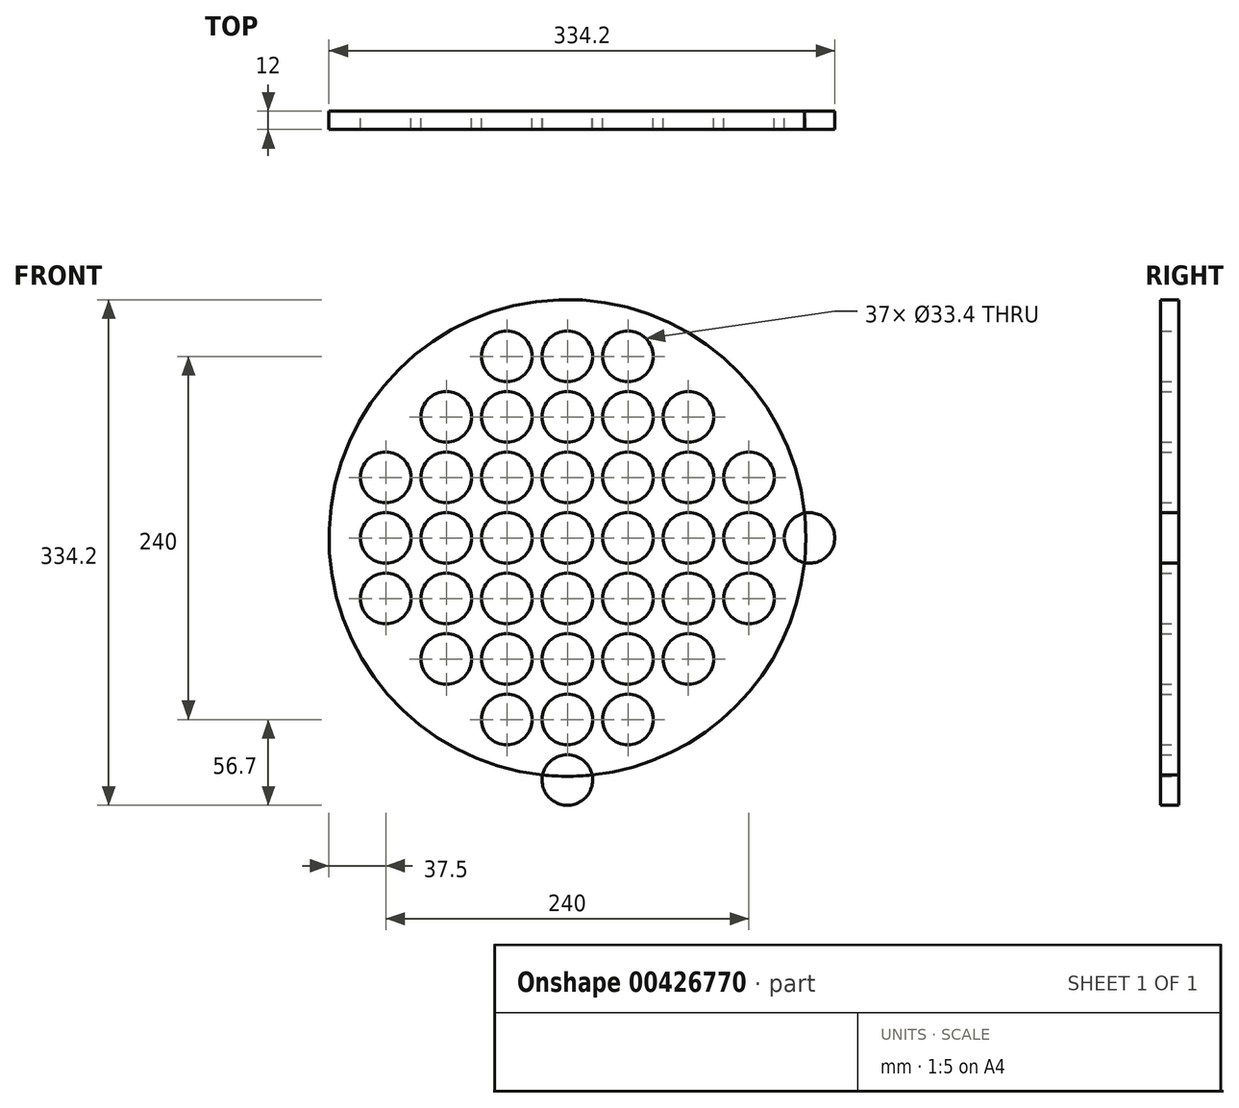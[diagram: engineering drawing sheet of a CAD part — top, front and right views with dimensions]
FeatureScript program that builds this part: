
annotation { "Feature Type Name" : "Feature", "Feature Type Description" : "" }
export const myFeature = defineFeature(function(context is Context, id is Id, definition is map)
    precondition{}
    {
        {
            var Q0;
            Q0=qCreatedBy(makeId("Front.planeOp"),FACE);
            var sketch = newSketch(context, id + "F0", { "sketchPlane" : qUnion([Q0])});
            skCircle(sketch, "E0", {"center": v(-240, -240) * mm, "radius": 16.7 * mm});
            skCircle(sketch, "E1.0.1.0", {"center": v(-240, -200) * mm, "radius": 16.7 * mm});
            skCircle(sketch, "E1.0.2.0", {"center": v(-240, -160) * mm, "radius": 16.7 * mm});
            skCircle(sketch, "E1.0.3.0", {"center": v(-240, -120) * mm, "radius": 16.7 * mm});
            skCircle(sketch, "E1.0.4.0", {"center": v(-240, -80) * mm, "radius": 16.7 * mm});
            skCircle(sketch, "E1.0.5.0", {"center": v(-240, -40) * mm, "radius": 16.7 * mm});
            skCircle(sketch, "E1.0.6.0", {"center": v(-240, 0) * mm, "radius": 16.7 * mm});
            skCircle(sketch, "E1.0.7.0", {"center": v(-240, 40) * mm, "radius": 16.7 * mm});
            skCircle(sketch, "E1.0.8.0", {"center": v(-240, 80) * mm, "radius": 16.7 * mm});
            skCircle(sketch, "E1.0.9.0", {"center": v(-240, 120) * mm, "radius": 16.7 * mm});
            skCircle(sketch, "E1.1.0.0", {"center": v(-200, -240) * mm, "radius": 16.7 * mm});
            skCircle(sketch, "E1.1.1.0", {"center": v(-200, -200) * mm, "radius": 16.7 * mm});
            skCircle(sketch, "E1.1.2.0", {"center": v(-200, -160) * mm, "radius": 16.7 * mm});
            skCircle(sketch, "E1.1.3.0", {"center": v(-200, -120) * mm, "radius": 16.7 * mm});
            skCircle(sketch, "E1.1.4.0", {"center": v(-200, -80) * mm, "radius": 16.7 * mm});
            skCircle(sketch, "E1.1.5.0", {"center": v(-200, -40) * mm, "radius": 16.7 * mm});
            skCircle(sketch, "E1.1.6.0", {"center": v(-200, 0) * mm, "radius": 16.7 * mm});
            skCircle(sketch, "E1.1.7.0", {"center": v(-200, 40) * mm, "radius": 16.7 * mm});
            skCircle(sketch, "E1.1.8.0", {"center": v(-200, 80) * mm, "radius": 16.7 * mm});
            skCircle(sketch, "E1.1.9.0", {"center": v(-200, 120) * mm, "radius": 16.7 * mm});
            skCircle(sketch, "E1.2.0.0", {"center": v(-160, -240) * mm, "radius": 16.7 * mm});
            skCircle(sketch, "E1.2.1.0", {"center": v(-160, -200) * mm, "radius": 16.7 * mm});
            skCircle(sketch, "E1.2.2.0", {"center": v(-160, -160) * mm, "radius": 16.7 * mm});
            skCircle(sketch, "E1.2.3.0", {"center": v(-160, -120) * mm, "radius": 16.7 * mm});
            skCircle(sketch, "E1.2.4.0", {"center": v(-160, -80) * mm, "radius": 16.7 * mm});
            skCircle(sketch, "E1.2.5.0", {"center": v(-160, -40) * mm, "radius": 16.7 * mm});
            skCircle(sketch, "E1.2.6.0", {"center": v(-160, 0) * mm, "radius": 16.7 * mm});
            skCircle(sketch, "E1.2.7.0", {"center": v(-160, 40) * mm, "radius": 16.7 * mm});
            skCircle(sketch, "E1.2.8.0", {"center": v(-160, 80) * mm, "radius": 16.7 * mm});
            skCircle(sketch, "E1.2.9.0", {"center": v(-160, 120) * mm, "radius": 16.7 * mm});
            skCircle(sketch, "E1.3.0.0", {"center": v(-120, -240) * mm, "radius": 16.7 * mm});
            skCircle(sketch, "E1.3.1.0", {"center": v(-120, -200) * mm, "radius": 16.7 * mm});
            skCircle(sketch, "E1.3.2.0", {"center": v(-120, -160) * mm, "radius": 16.7 * mm});
            skCircle(sketch, "E1.3.3.0", {"center": v(-120, -120) * mm, "radius": 16.7 * mm});
            skCircle(sketch, "E1.3.4.0", {"center": v(-120, -80) * mm, "radius": 16.7 * mm});
            skCircle(sketch, "E1.3.5.0", {"center": v(-120, -40) * mm, "radius": 16.7 * mm});
            skCircle(sketch, "E1.3.6.0", {"center": v(-120, 0) * mm, "radius": 16.7 * mm});
            skCircle(sketch, "E1.3.7.0", {"center": v(-120, 40) * mm, "radius": 16.7 * mm});
            skCircle(sketch, "E1.3.8.0", {"center": v(-120, 80) * mm, "radius": 16.7 * mm});
            skCircle(sketch, "E1.3.9.0", {"center": v(-120, 120) * mm, "radius": 16.7 * mm});
            skCircle(sketch, "E1.4.0.0", {"center": v(-80, -240) * mm, "radius": 16.7 * mm});
            skCircle(sketch, "E1.4.1.0", {"center": v(-80, -200) * mm, "radius": 16.7 * mm});
            skCircle(sketch, "E1.4.2.0", {"center": v(-80, -160) * mm, "radius": 16.7 * mm});
            skCircle(sketch, "E1.4.3.0", {"center": v(-80, -120) * mm, "radius": 16.7 * mm});
            skCircle(sketch, "E1.4.4.0", {"center": v(-80, -80) * mm, "radius": 16.7 * mm});
            skCircle(sketch, "E1.4.5.0", {"center": v(-80, -40) * mm, "radius": 16.7 * mm});
            skCircle(sketch, "E1.4.6.0", {"center": v(-80, 0) * mm, "radius": 16.7 * mm});
            skCircle(sketch, "E1.4.7.0", {"center": v(-80, 40) * mm, "radius": 16.7 * mm});
            skCircle(sketch, "E1.4.8.0", {"center": v(-80, 80) * mm, "radius": 16.7 * mm});
            skCircle(sketch, "E1.4.9.0", {"center": v(-80, 120) * mm, "radius": 16.7 * mm});
            skCircle(sketch, "E1.5.0.0", {"center": v(-40, -240) * mm, "radius": 16.7 * mm});
            skCircle(sketch, "E1.5.1.0", {"center": v(-40, -200) * mm, "radius": 16.7 * mm});
            skCircle(sketch, "E1.5.2.0", {"center": v(-40, -160) * mm, "radius": 16.7 * mm});
            skCircle(sketch, "E1.5.3.0", {"center": v(-40, -120) * mm, "radius": 16.7 * mm});
            skCircle(sketch, "E1.5.4.0", {"center": v(-40, -80) * mm, "radius": 16.7 * mm});
            skCircle(sketch, "E1.5.5.0", {"center": v(-40, -40) * mm, "radius": 16.7 * mm});
            skCircle(sketch, "E1.5.6.0", {"center": v(-40, 0) * mm, "radius": 16.7 * mm});
            skCircle(sketch, "E1.5.7.0", {"center": v(-40, 40) * mm, "radius": 16.7 * mm});
            skCircle(sketch, "E1.5.8.0", {"center": v(-40, 80) * mm, "radius": 16.7 * mm});
            skCircle(sketch, "E1.5.9.0", {"center": v(-40, 120) * mm, "radius": 16.7 * mm});
            skCircle(sketch, "E1.6.0.0", {"center": v(0, -240) * mm, "radius": 16.7 * mm});
            skCircle(sketch, "E1.6.1.0", {"center": v(0, -200) * mm, "radius": 16.7 * mm});
            skCircle(sketch, "E1.6.2.0", {"center": v(0, -160) * mm, "radius": 16.7 * mm});
            skCircle(sketch, "E1.6.3.0", {"center": v(0, -120) * mm, "radius": 16.7 * mm});
            skCircle(sketch, "E1.6.4.0", {"center": v(0, -80) * mm, "radius": 16.7 * mm});
            skCircle(sketch, "E1.6.5.0", {"center": v(0, -40) * mm, "radius": 16.7 * mm});
            skCircle(sketch, "E1.6.6.0", {"center": v(0, 0) * mm, "radius": 16.7 * mm});
            skCircle(sketch, "E1.6.7.0", {"center": v(0, 40) * mm, "radius": 16.7 * mm});
            skCircle(sketch, "E1.6.8.0", {"center": v(0, 80) * mm, "radius": 16.7 * mm});
            skCircle(sketch, "E1.6.9.0", {"center": v(0, 120) * mm, "radius": 16.7 * mm});
            skCircle(sketch, "E1.7.0.0", {"center": v(40, -240) * mm, "radius": 16.7 * mm});
            skCircle(sketch, "E1.7.1.0", {"center": v(40, -200) * mm, "radius": 16.7 * mm});
            skCircle(sketch, "E1.7.2.0", {"center": v(40, -160) * mm, "radius": 16.7 * mm});
            skCircle(sketch, "E1.7.3.0", {"center": v(40, -120) * mm, "radius": 16.7 * mm});
            skCircle(sketch, "E1.7.4.0", {"center": v(40, -80) * mm, "radius": 16.7 * mm});
            skCircle(sketch, "E1.7.5.0", {"center": v(40, -40) * mm, "radius": 16.7 * mm});
            skCircle(sketch, "E1.7.6.0", {"center": v(40, 0) * mm, "radius": 16.7 * mm});
            skCircle(sketch, "E1.7.7.0", {"center": v(40, 40) * mm, "radius": 16.7 * mm});
            skCircle(sketch, "E1.7.8.0", {"center": v(40, 80) * mm, "radius": 16.7 * mm});
            skCircle(sketch, "E1.7.9.0", {"center": v(40, 120) * mm, "radius": 16.7 * mm});
            skCircle(sketch, "E1.8.0.0", {"center": v(80, -240) * mm, "radius": 16.7 * mm});
            skCircle(sketch, "E1.8.1.0", {"center": v(80, -200) * mm, "radius": 16.7 * mm});
            skCircle(sketch, "E1.8.2.0", {"center": v(80, -160) * mm, "radius": 16.7 * mm});
            skCircle(sketch, "E1.8.3.0", {"center": v(80, -120) * mm, "radius": 16.7 * mm});
            skCircle(sketch, "E1.8.4.0", {"center": v(80, -80) * mm, "radius": 16.7 * mm});
            skCircle(sketch, "E1.8.5.0", {"center": v(80, -40) * mm, "radius": 16.7 * mm});
            skCircle(sketch, "E1.8.6.0", {"center": v(80, 0) * mm, "radius": 16.7 * mm});
            skCircle(sketch, "E1.8.7.0", {"center": v(80, 40) * mm, "radius": 16.7 * mm});
            skCircle(sketch, "E1.8.8.0", {"center": v(80, 80) * mm, "radius": 16.7 * mm});
            skCircle(sketch, "E1.8.9.0", {"center": v(80, 120) * mm, "radius": 16.7 * mm});
            skCircle(sketch, "E1.9.0.0", {"center": v(120, -240) * mm, "radius": 16.7 * mm});
            skCircle(sketch, "E1.9.1.0", {"center": v(120, -200) * mm, "radius": 16.7 * mm});
            skCircle(sketch, "E1.9.2.0", {"center": v(120, -160) * mm, "radius": 16.7 * mm});
            skCircle(sketch, "E1.9.3.0", {"center": v(120, -120) * mm, "radius": 16.7 * mm});
            skCircle(sketch, "E1.9.4.0", {"center": v(120, -80) * mm, "radius": 16.7 * mm});
            skCircle(sketch, "E1.9.5.0", {"center": v(120, -40) * mm, "radius": 16.7 * mm});
            skCircle(sketch, "E1.9.6.0", {"center": v(120, 0) * mm, "radius": 16.7 * mm});
            skCircle(sketch, "E1.9.7.0", {"center": v(120, 40) * mm, "radius": 16.7 * mm});
            skCircle(sketch, "E1.9.8.0", {"center": v(120, 80) * mm, "radius": 16.7 * mm});
            skCircle(sketch, "E1.9.9.0", {"center": v(120, 120) * mm, "radius": 16.7 * mm});
            skLineSegment(sketch, "E1.direction1", {"start": v(-240, -240) * mm, "end": v(-200, -240) * mm, "construction": true});
            skLineSegment(sketch, "E1.direction2", {"start": v(-240, -240) * mm, "end": v(-240, -200) * mm, "construction": true});
            skCircle(sketch, "E2.0.0.10", {"center": v(-240, 160) * mm, "radius": 16.7 * mm});
            skCircle(sketch, "E2.0.0.11", {"center": v(-240, 200) * mm, "radius": 16.7 * mm});
            skCircle(sketch, "E2.0.1.10", {"center": v(-200, 160) * mm, "radius": 16.7 * mm});
            skCircle(sketch, "E2.0.1.11", {"center": v(-200, 200) * mm, "radius": 16.7 * mm});
            skCircle(sketch, "E2.0.2.10", {"center": v(-160, 160) * mm, "radius": 16.7 * mm});
            skCircle(sketch, "E2.0.2.11", {"center": v(-160, 200) * mm, "radius": 16.7 * mm});
            skCircle(sketch, "E2.0.3.10", {"center": v(-120, 160) * mm, "radius": 16.7 * mm});
            skCircle(sketch, "E2.0.3.11", {"center": v(-120, 200) * mm, "radius": 16.7 * mm});
            skCircle(sketch, "E2.0.4.10", {"center": v(-80, 160) * mm, "radius": 16.7 * mm});
            skCircle(sketch, "E2.0.4.11", {"center": v(-80, 200) * mm, "radius": 16.7 * mm});
            skCircle(sketch, "E2.0.5.10", {"center": v(-40, 160) * mm, "radius": 16.7 * mm});
            skCircle(sketch, "E2.0.5.11", {"center": v(-40, 200) * mm, "radius": 16.7 * mm});
            skCircle(sketch, "E2.0.6.10", {"center": v(0, 160) * mm, "radius": 16.7 * mm});
            skCircle(sketch, "E2.0.6.11", {"center": v(0, 200) * mm, "radius": 16.7 * mm});
            skCircle(sketch, "E2.0.7.10", {"center": v(40, 160) * mm, "radius": 16.7 * mm});
            skCircle(sketch, "E2.0.7.11", {"center": v(40, 200) * mm, "radius": 16.7 * mm});
            skCircle(sketch, "E2.0.8.10", {"center": v(80, 160) * mm, "radius": 16.7 * mm});
            skCircle(sketch, "E2.0.8.11", {"center": v(80, 200) * mm, "radius": 16.7 * mm});
            skCircle(sketch, "E2.0.9.10", {"center": v(120, 160) * mm, "radius": 16.7 * mm});
            skCircle(sketch, "E2.0.9.11", {"center": v(120, 200) * mm, "radius": 16.7 * mm});
            skCircle(sketch, "E3.0.10.0", {"center": v(160, -240) * mm, "radius": 16.7 * mm});
            skCircle(sketch, "E3.0.10.1", {"center": v(160, -200) * mm, "radius": 16.7 * mm});
            skCircle(sketch, "E3.0.10.2", {"center": v(160, -160) * mm, "radius": 16.7 * mm});
            skCircle(sketch, "E3.0.10.3", {"center": v(160, -120) * mm, "radius": 16.7 * mm});
            skCircle(sketch, "E3.0.10.4", {"center": v(160, -80) * mm, "radius": 16.7 * mm});
            skCircle(sketch, "E3.0.10.5", {"center": v(160, -40) * mm, "radius": 16.7 * mm});
            skCircle(sketch, "E3.0.10.6", {"center": v(160, 0) * mm, "radius": 16.7 * mm});
            skCircle(sketch, "E3.0.10.7", {"center": v(160, 40) * mm, "radius": 16.7 * mm});
            skCircle(sketch, "E3.0.10.8", {"center": v(160, 80) * mm, "radius": 16.7 * mm});
            skCircle(sketch, "E3.0.10.9", {"center": v(160, 120) * mm, "radius": 16.7 * mm});
            skCircle(sketch, "E3.0.10.10", {"center": v(160, 160) * mm, "radius": 16.7 * mm});
            skCircle(sketch, "E3.0.10.11", {"center": v(160, 200) * mm, "radius": 16.7 * mm});
            skCircle(sketch, "E3.0.11.0", {"center": v(200, -240) * mm, "radius": 16.7 * mm});
            skCircle(sketch, "E3.0.11.1", {"center": v(200, -200) * mm, "radius": 16.7 * mm});
            skCircle(sketch, "E3.0.11.2", {"center": v(200, -160) * mm, "radius": 16.7 * mm});
            skCircle(sketch, "E3.0.11.3", {"center": v(200, -120) * mm, "radius": 16.7 * mm});
            skCircle(sketch, "E3.0.11.4", {"center": v(200, -80) * mm, "radius": 16.7 * mm});
            skCircle(sketch, "E3.0.11.5", {"center": v(200, -40) * mm, "radius": 16.7 * mm});
            skCircle(sketch, "E3.0.11.6", {"center": v(200, 0) * mm, "radius": 16.7 * mm});
            skCircle(sketch, "E3.0.11.7", {"center": v(200, 40) * mm, "radius": 16.7 * mm});
            skCircle(sketch, "E3.0.11.8", {"center": v(200, 80) * mm, "radius": 16.7 * mm});
            skCircle(sketch, "E3.0.11.9", {"center": v(200, 120) * mm, "radius": 16.7 * mm});
            skCircle(sketch, "E3.0.11.10", {"center": v(200, 160) * mm, "radius": 16.7 * mm});
            skCircle(sketch, "E3.0.11.11", {"center": v(200, 200) * mm, "radius": 16.7 * mm});
            skCircle(sketch, "E4.0.0.12", {"center": v(-240, 240) * mm, "radius": 16.7 * mm});
            skCircle(sketch, "E4.0.1.12", {"center": v(-200, 240) * mm, "radius": 16.7 * mm});
            skCircle(sketch, "E4.0.2.12", {"center": v(-160, 240) * mm, "radius": 16.7 * mm});
            skCircle(sketch, "E4.0.3.12", {"center": v(-120, 240) * mm, "radius": 16.7 * mm});
            skCircle(sketch, "E4.0.4.12", {"center": v(-80, 240) * mm, "radius": 16.7 * mm});
            skCircle(sketch, "E4.0.5.12", {"center": v(-40, 240) * mm, "radius": 16.7 * mm});
            skCircle(sketch, "E4.0.6.12", {"center": v(0, 240) * mm, "radius": 16.7 * mm});
            skCircle(sketch, "E4.0.7.12", {"center": v(40, 240) * mm, "radius": 16.7 * mm});
            skCircle(sketch, "E4.0.8.12", {"center": v(80, 240) * mm, "radius": 16.7 * mm});
            skCircle(sketch, "E4.0.9.12", {"center": v(120, 240) * mm, "radius": 16.7 * mm});
            skCircle(sketch, "E4.0.10.12", {"center": v(160, 240) * mm, "radius": 16.7 * mm});
            skCircle(sketch, "E4.0.11.12", {"center": v(200, 240) * mm, "radius": 16.7 * mm});
            skCircle(sketch, "E5.0.12.0", {"center": v(240, -240) * mm, "radius": 16.7 * mm});
            skCircle(sketch, "E5.0.12.1", {"center": v(240, -200) * mm, "radius": 16.7 * mm});
            skCircle(sketch, "E5.0.12.2", {"center": v(240, -160) * mm, "radius": 16.7 * mm});
            skCircle(sketch, "E5.0.12.3", {"center": v(240, -120) * mm, "radius": 16.7 * mm});
            skCircle(sketch, "E5.0.12.4", {"center": v(240, -80) * mm, "radius": 16.7 * mm});
            skCircle(sketch, "E5.0.12.5", {"center": v(240, -40) * mm, "radius": 16.7 * mm});
            skCircle(sketch, "E5.0.12.6", {"center": v(240, 0) * mm, "radius": 16.7 * mm});
            skCircle(sketch, "E5.0.12.7", {"center": v(240, 40) * mm, "radius": 16.7 * mm});
            skCircle(sketch, "E5.0.12.8", {"center": v(240, 80) * mm, "radius": 16.7 * mm});
            skCircle(sketch, "E5.0.12.9", {"center": v(240, 120) * mm, "radius": 16.7 * mm});
            skCircle(sketch, "E5.0.12.10", {"center": v(240, 160) * mm, "radius": 16.7 * mm});
            skCircle(sketch, "E5.0.12.11", {"center": v(240, 200) * mm, "radius": 16.7 * mm});
            skCircle(sketch, "E5.0.12.12", {"center": v(240, 240) * mm, "radius": 16.7 * mm});
            skCircle(sketch, "E6", {"center": v(0, 0) * mm, "radius": 157.5 * mm});
            skSolve(sketch);
        }
        {
            var Q0;
            Q0=makeQuery(id+"F0.imprint","IMPRINT",FACE,{"disambiguationData":[TD([[makeQuery(id+"F0.imprint","IMPRINT",EDGE,{"derivedFrom":sQuery(id+"F0.wireOp",EDGE,"E1.3.5.0")}),-1.0]])]});
            var Q1;
            {var subQ0=sQuery(id+"F0.wireOp",EDGE,"E6");var subQ1=sQuery(id+"F0.wireOp",EDGE,"E2.0.5.10");var subQ2=makeQuery(id+"F0.imprint","INTERSECT",VERTEX,{"disambiguationData":[OD(0.0)],"derivedFrom":[subQ1,subQ0]});Q1=makeQuery(id+"F0.imprint","IMPRINT",FACE,{"disambiguationData":[TD([[makeQuery(id+"F0.imprint","IMPRINT",EDGE,{"disambiguationData":[TD([[subQ2,1.0]])],"derivedFrom":subQ1}),1.0]])]});}
            var Q2;
            {var subQ0=sQuery(id+"F0.wireOp",EDGE,"E6");var subQ1=sQuery(id+"F0.wireOp",EDGE,"E2.0.6.10");var subQ2=makeQuery(id+"F0.imprint","INTERSECT",VERTEX,{"disambiguationData":[OD(0.0)],"derivedFrom":[subQ1,subQ0]});Q2=makeQuery(id+"F0.imprint","IMPRINT",FACE,{"disambiguationData":[TD([[makeQuery(id+"F0.imprint","IMPRINT",EDGE,{"disambiguationData":[TD([[subQ2,1.0]])],"derivedFrom":subQ1}),1.0]])]});}
            var Q3;
            {var subQ0=sQuery(id+"F0.wireOp",EDGE,"E6");var subQ1=sQuery(id+"F0.wireOp",EDGE,"E2.0.7.10");var subQ2=makeQuery(id+"F0.imprint","INTERSECT",VERTEX,{"disambiguationData":[OD(0.0)],"derivedFrom":[subQ1,subQ0]});Q3=makeQuery(id+"F0.imprint","IMPRINT",FACE,{"disambiguationData":[TD([[makeQuery(id+"F0.imprint","IMPRINT",EDGE,{"disambiguationData":[TD([[subQ2,1.0]])],"derivedFrom":subQ1}),1.0]])]});}
            var Q4;
            {var subQ0=sQuery(id+"F0.wireOp",EDGE,"E6");var subQ1=sQuery(id+"F0.wireOp",EDGE,"E1.8.9.0");var subQ2=makeQuery(id+"F0.imprint","INTERSECT",VERTEX,{"disambiguationData":[OD(0.0)],"derivedFrom":[subQ1,subQ0]});Q4=makeQuery(id+"F0.imprint","IMPRINT",FACE,{"disambiguationData":[TD([[makeQuery(id+"F0.imprint","IMPRINT",EDGE,{"disambiguationData":[TD([[subQ2,1.0]])],"derivedFrom":subQ1}),1.0]])]});}
            var Q5;
            {var subQ0=sQuery(id+"F0.wireOp",EDGE,"E6");var subQ1=sQuery(id+"F0.wireOp",EDGE,"E1.9.9.0");var subQ2=makeQuery(id+"F0.imprint","INTERSECT",VERTEX,{"disambiguationData":[OD(0.0)],"derivedFrom":[subQ1,subQ0]});Q5=makeQuery(id+"F0.imprint","IMPRINT",FACE,{"disambiguationData":[TD([[makeQuery(id+"F0.imprint","IMPRINT",EDGE,{"disambiguationData":[TD([[subQ2,1.0]])],"derivedFrom":subQ1}),1.0]])]});}
            var Q6;
            {var subQ0=sQuery(id+"F0.wireOp",EDGE,"E6");var subQ1=sQuery(id+"F0.wireOp",EDGE,"E1.4.9.0");var subQ2=makeQuery(id+"F0.imprint","INTERSECT",VERTEX,{"disambiguationData":[OD(0.0)],"derivedFrom":[subQ1,subQ0]});Q6=makeQuery(id+"F0.imprint","IMPRINT",FACE,{"disambiguationData":[TD([[makeQuery(id+"F0.imprint","IMPRINT",EDGE,{"disambiguationData":[TD([[subQ2,1.0]])],"derivedFrom":subQ1}),1.0]])]});}
            var Q7;
            {var subQ0=sQuery(id+"F0.wireOp",EDGE,"E6");var subQ1=sQuery(id+"F0.wireOp",EDGE,"E1.3.9.0");var subQ2=makeQuery(id+"F0.imprint","INTERSECT",VERTEX,{"disambiguationData":[OD(0.0)],"derivedFrom":[subQ1,subQ0]});Q7=makeQuery(id+"F0.imprint","IMPRINT",FACE,{"disambiguationData":[TD([[makeQuery(id+"F0.imprint","IMPRINT",EDGE,{"disambiguationData":[TD([[subQ2,1.0]])],"derivedFrom":subQ1}),1.0]])]});}
            var Q8;
            {var subQ0=sQuery(id+"F0.wireOp",EDGE,"E6");var subQ1=sQuery(id+"F0.wireOp",EDGE,"E1.3.8.0");var subQ2=makeQuery(id+"F0.imprint","INTERSECT",VERTEX,{"disambiguationData":[OD(0.0)],"derivedFrom":[subQ1,subQ0]});Q8=makeQuery(id+"F0.imprint","IMPRINT",FACE,{"disambiguationData":[TD([[makeQuery(id+"F0.imprint","IMPRINT",EDGE,{"disambiguationData":[TD([[subQ2,1.0]])],"derivedFrom":subQ1}),1.0]])]});}
            var Q9;
            {var subQ0=sQuery(id+"F0.wireOp",EDGE,"E6");var subQ1=sQuery(id+"F0.wireOp",EDGE,"E1.9.8.0");var subQ2=makeQuery(id+"F0.imprint","INTERSECT",VERTEX,{"disambiguationData":[OD(0.0)],"derivedFrom":[subQ1,subQ0]});Q9=makeQuery(id+"F0.imprint","IMPRINT",FACE,{"disambiguationData":[TD([[makeQuery(id+"F0.imprint","IMPRINT",EDGE,{"disambiguationData":[TD([[subQ2,1.0]])],"derivedFrom":subQ1}),1.0]])]});}
            var Q10;
            {var subQ0=sQuery(id+"F0.wireOp",EDGE,"E6");var subQ1=sQuery(id+"F0.wireOp",EDGE,"E3.0.10.7");var subQ2=makeQuery(id+"F0.imprint","INTERSECT",VERTEX,{"disambiguationData":[OD(0.0)],"derivedFrom":[subQ1,subQ0]});Q10=makeQuery(id+"F0.imprint","IMPRINT",FACE,{"disambiguationData":[TD([[makeQuery(id+"F0.imprint","IMPRINT",EDGE,{"disambiguationData":[TD([[subQ2,1.0]])],"derivedFrom":subQ1}),1.0]])]});}
            var Q11;
            {var subQ0=sQuery(id+"F0.wireOp",EDGE,"E6");var subQ1=sQuery(id+"F0.wireOp",EDGE,"E3.0.10.6");var subQ2=makeQuery(id+"F0.imprint","INTERSECT",VERTEX,{"disambiguationData":[OD(0.0)],"derivedFrom":[subQ1,subQ0]});Q11=makeQuery(id+"F0.imprint","IMPRINT",FACE,{"disambiguationData":[TD([[makeQuery(id+"F0.imprint","IMPRINT",EDGE,{"disambiguationData":[TD([[subQ2,-1.0]])],"derivedFrom":subQ1}),1.0]])]});}
            var Q12;
            {var subQ0=sQuery(id+"F0.wireOp",EDGE,"E6");var subQ1=sQuery(id+"F0.wireOp",EDGE,"E3.0.10.5");var subQ2=makeQuery(id+"F0.imprint","INTERSECT",VERTEX,{"disambiguationData":[OD(0.0)],"derivedFrom":[subQ1,subQ0]});Q12=makeQuery(id+"F0.imprint","IMPRINT",FACE,{"disambiguationData":[TD([[makeQuery(id+"F0.imprint","IMPRINT",EDGE,{"disambiguationData":[TD([[subQ2,1.0]])],"derivedFrom":subQ1}),1.0]])]});}
            var Q13;
            {var subQ0=sQuery(id+"F0.wireOp",EDGE,"E6");var subQ1=sQuery(id+"F0.wireOp",EDGE,"E1.9.4.0");var subQ2=makeQuery(id+"F0.imprint","INTERSECT",VERTEX,{"disambiguationData":[OD(0.0)],"derivedFrom":[subQ1,subQ0]});Q13=makeQuery(id+"F0.imprint","IMPRINT",FACE,{"disambiguationData":[TD([[makeQuery(id+"F0.imprint","IMPRINT",EDGE,{"disambiguationData":[TD([[subQ2,1.0]])],"derivedFrom":subQ1}),1.0]])]});}
            var Q14;
            {var subQ0=sQuery(id+"F0.wireOp",EDGE,"E6");var subQ1=sQuery(id+"F0.wireOp",EDGE,"E1.9.3.0");var subQ2=makeQuery(id+"F0.imprint","INTERSECT",VERTEX,{"disambiguationData":[OD(0.0)],"derivedFrom":[subQ1,subQ0]});Q14=makeQuery(id+"F0.imprint","IMPRINT",FACE,{"disambiguationData":[TD([[makeQuery(id+"F0.imprint","IMPRINT",EDGE,{"disambiguationData":[TD([[subQ2,1.0]])],"derivedFrom":subQ1}),1.0]])]});}
            var Q15;
            {var subQ0=sQuery(id+"F0.wireOp",EDGE,"E6");var subQ1=sQuery(id+"F0.wireOp",EDGE,"E1.8.3.0");var subQ2=makeQuery(id+"F0.imprint","INTERSECT",VERTEX,{"disambiguationData":[OD(0.0)],"derivedFrom":[subQ1,subQ0]});Q15=makeQuery(id+"F0.imprint","IMPRINT",FACE,{"disambiguationData":[TD([[makeQuery(id+"F0.imprint","IMPRINT",EDGE,{"disambiguationData":[TD([[subQ2,1.0]])],"derivedFrom":subQ1}),1.0]])]});}
            var Q16;
            {var subQ0=sQuery(id+"F0.wireOp",EDGE,"E6");var subQ1=sQuery(id+"F0.wireOp",EDGE,"E1.7.2.0");var subQ2=makeQuery(id+"F0.imprint","INTERSECT",VERTEX,{"disambiguationData":[OD(0.0)],"derivedFrom":[subQ1,subQ0]});Q16=makeQuery(id+"F0.imprint","IMPRINT",FACE,{"disambiguationData":[TD([[makeQuery(id+"F0.imprint","IMPRINT",EDGE,{"disambiguationData":[TD([[subQ2,1.0]])],"derivedFrom":subQ1}),1.0]])]});}
            var Q17;
            {var subQ0=sQuery(id+"F0.wireOp",EDGE,"E6");var subQ1=sQuery(id+"F0.wireOp",EDGE,"E1.6.2.0");var subQ2=makeQuery(id+"F0.imprint","INTERSECT",VERTEX,{"disambiguationData":[OD(0.0)],"derivedFrom":[subQ1,subQ0]});Q17=makeQuery(id+"F0.imprint","IMPRINT",FACE,{"disambiguationData":[TD([[makeQuery(id+"F0.imprint","IMPRINT",EDGE,{"disambiguationData":[TD([[subQ2,1.0]])],"derivedFrom":subQ1}),1.0]])]});}
            var Q18;
            {var subQ0=sQuery(id+"F0.wireOp",EDGE,"E6");var subQ1=sQuery(id+"F0.wireOp",EDGE,"E1.5.2.0");var subQ2=makeQuery(id+"F0.imprint","INTERSECT",VERTEX,{"disambiguationData":[OD(0.0)],"derivedFrom":[subQ1,subQ0]});Q18=makeQuery(id+"F0.imprint","IMPRINT",FACE,{"disambiguationData":[TD([[makeQuery(id+"F0.imprint","IMPRINT",EDGE,{"disambiguationData":[TD([[subQ2,1.0]])],"derivedFrom":subQ1}),1.0]])]});}
            var Q19;
            {var subQ0=sQuery(id+"F0.wireOp",EDGE,"E6");var subQ1=sQuery(id+"F0.wireOp",EDGE,"E1.4.3.0");var subQ2=makeQuery(id+"F0.imprint","INTERSECT",VERTEX,{"disambiguationData":[OD(0.0)],"derivedFrom":[subQ1,subQ0]});Q19=makeQuery(id+"F0.imprint","IMPRINT",FACE,{"disambiguationData":[TD([[makeQuery(id+"F0.imprint","IMPRINT",EDGE,{"disambiguationData":[TD([[subQ2,1.0]])],"derivedFrom":subQ1}),1.0]])]});}
            var Q20;
            {var subQ0=sQuery(id+"F0.wireOp",EDGE,"E6");var subQ1=sQuery(id+"F0.wireOp",EDGE,"E1.3.4.0");var subQ2=makeQuery(id+"F0.imprint","INTERSECT",VERTEX,{"disambiguationData":[OD(0.0)],"derivedFrom":[subQ1,subQ0]});Q20=makeQuery(id+"F0.imprint","IMPRINT",FACE,{"disambiguationData":[TD([[makeQuery(id+"F0.imprint","IMPRINT",EDGE,{"disambiguationData":[TD([[subQ2,1.0]])],"derivedFrom":subQ1}),1.0]])]});}
            var Q21;
            {var subQ0=sQuery(id+"F0.wireOp",EDGE,"E6");var subQ1=sQuery(id+"F0.wireOp",EDGE,"E1.2.5.0");var subQ2=makeQuery(id+"F0.imprint","INTERSECT",VERTEX,{"disambiguationData":[OD(0.0)],"derivedFrom":[subQ1,subQ0]});Q21=makeQuery(id+"F0.imprint","IMPRINT",FACE,{"disambiguationData":[TD([[makeQuery(id+"F0.imprint","IMPRINT",EDGE,{"disambiguationData":[TD([[subQ2,1.0]])],"derivedFrom":subQ1}),1.0]])]});}
            var Q22;
            {var subQ0=sQuery(id+"F0.wireOp",EDGE,"E6");var subQ1=sQuery(id+"F0.wireOp",EDGE,"E1.2.6.0");var subQ2=makeQuery(id+"F0.imprint","INTERSECT",VERTEX,{"disambiguationData":[OD(0.0)],"derivedFrom":[subQ1,subQ0]});Q22=makeQuery(id+"F0.imprint","IMPRINT",FACE,{"disambiguationData":[TD([[makeQuery(id+"F0.imprint","IMPRINT",EDGE,{"disambiguationData":[TD([[subQ2,1.0]])],"derivedFrom":subQ1}),1.0]])]});}
            var Q23;
            {var subQ0=sQuery(id+"F0.wireOp",EDGE,"E6");var subQ1=sQuery(id+"F0.wireOp",EDGE,"E1.2.7.0");var subQ2=makeQuery(id+"F0.imprint","INTERSECT",VERTEX,{"disambiguationData":[OD(0.0)],"derivedFrom":[subQ1,subQ0]});Q23=makeQuery(id+"F0.imprint","IMPRINT",FACE,{"disambiguationData":[TD([[makeQuery(id+"F0.imprint","IMPRINT",EDGE,{"disambiguationData":[TD([[subQ2,1.0]])],"derivedFrom":subQ1}),1.0]])]});}
            var Q24;
            {var subQ0=sQuery(id+"F0.wireOp",EDGE,"E6");var subQ1=sQuery(id+"F0.wireOp",EDGE,"E1.3.3.0");var subQ2=makeQuery(id+"F0.imprint","INTERSECT",VERTEX,{"disambiguationData":[OD(0.0)],"derivedFrom":[subQ1,subQ0]});Q24=makeQuery(id+"F0.imprint","IMPRINT",FACE,{"disambiguationData":[TD([[makeQuery(id+"F0.imprint","IMPRINT",EDGE,{"disambiguationData":[TD([[subQ2,1.0]])],"derivedFrom":subQ1}),1.0]])]});}
            extrude(context, id + "F1", {"entities" : qUnion([Q0, Q1, Q2, Q3, Q4, Q5, Q6, Q7, Q8, Q9, Q10, Q11, Q12, Q13, Q14, Q15, Q16, Q17, Q18, Q19, Q20, Q21, Q22, Q23, Q24]), "depth" : 12 * mm});
        }
    });
